# Revit family: Dio
name_source: partatom
category: Lighting Fixtures
revit_build: Autodesk Revit 2018 (Build: 20170223_1515(x64)
units: mm (PartAtom-declared; Revit-internal decimal feet)

## family parameters
Cut with Voids When Loaded = No
Host = Face
Light Source = Yes
OmniClass Number = 23.80.70.00
OmniClass Title = Lighting
Part Type = Normal
Room Calculation Point = No
Round Connector Dimension = Use Diameter
Shared = No

## types (1)
- 1305006 Dio
    Apparent Load = 17 VA
    Assembly Code = D5020200
    Casing Material = Astro - Aluminium - Chrome Finish
    Class = 2
    Color Filter = 16777215
    Description = GNC-1796 Dio.ies
    Dimmable = No
    Dimming Lamp Color Temperature Shift = <None>
    Emit from Line Length = 609.6 mm  [stored 2 ft]
    Height = 40 mm  [stored 0.131234 ft]
    IP Rating = IP44
    Lamp = LED
    Lamp included = No
    Length = 90 mm  [stored 0.295276 ft]
    Light Source From Wall = 70 mm  [stored 0.229659 ft]
    Manufacturer = Astro Lighting Ltd, CM20 2DP
    Model = 7101 Dio
    Mountable on normally flammable surfaces = Yes
    Number of Poles = 1
    Photometric Web File = GNC-1796 Dio.ies
    Product Documentation = http://www.astrolighting.co.uk
    Suitable for bathroom zone = Zones 2 and 3
    Tilt Angle = 90.00°
    Type Comments = Includes integral LED driver. Can be mounted horizontally or vertically.
    URL = www.astrolighting.co.uk
    Voltage = 230 V
    Wattage Comments = 6.4w
    Weight = 0.8kg
    Width = 340 mm  [stored 1.11549 ft]

note: [stored X ft] marks values corroborated as IEEE doubles in the binary element streams (Revit-internal decimal feet)

## geometry (parser evidence)
native form markers: Sweep x2
no freeform markers — native parametric forms only
